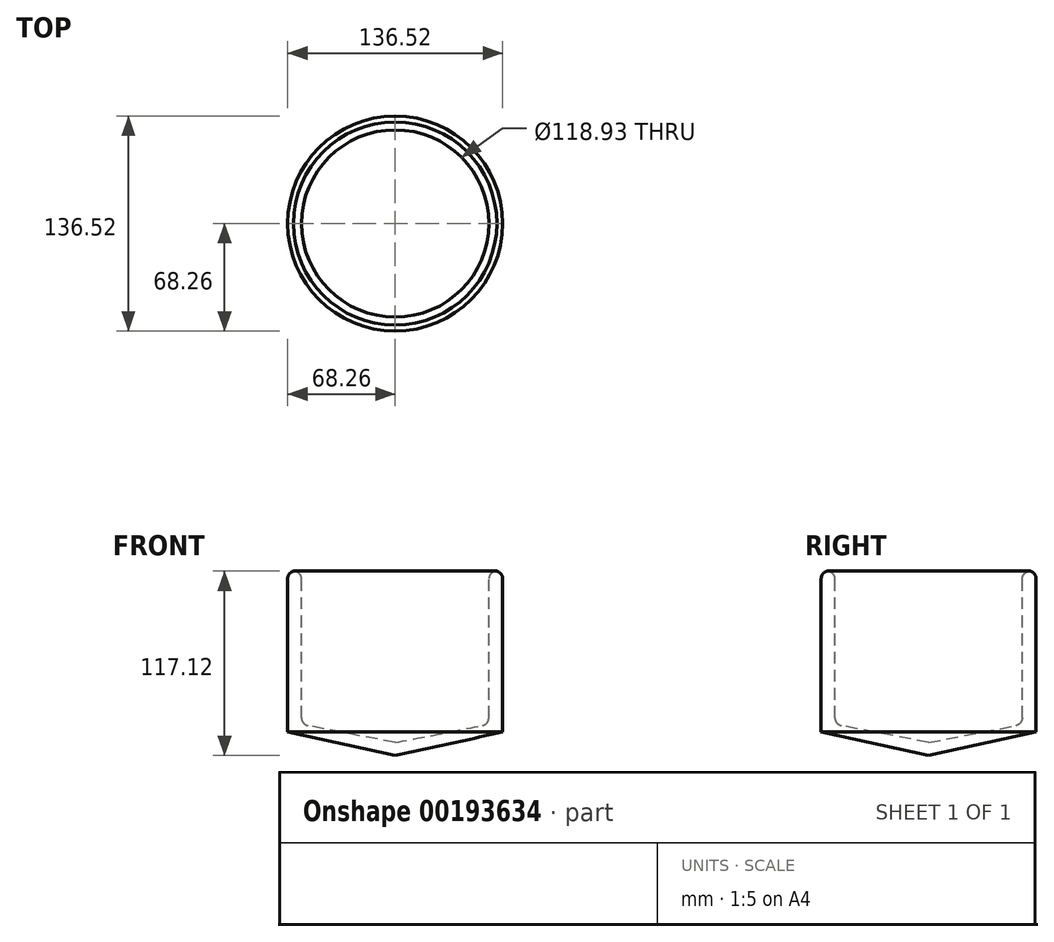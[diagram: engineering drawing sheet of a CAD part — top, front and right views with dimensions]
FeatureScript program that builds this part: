
annotation { "Feature Type Name" : "Feature", "Feature Type Description" : "" }
export const myFeature = defineFeature(function(context is Context, id is Id, definition is map)
    precondition{}
    {
        {
            var Q0;
            Q0=qCreatedBy(makeId("Front.planeOp"),FACE);
            var sketch = newSketch(context, id + "F0", { "sketchPlane" : qUnion([Q0])});
            skLineSegment(sketch, "E0", {"start": v(0, 62.05) * mm, "end": v(0, -60.22) * mm});
            skLineSegment(sketch, "E1", {"start": v(59.47, 48.7) * mm, "end": v(59.47, -48.7) * mm});
            skLineSegment(sketch, "E2", {"start": v(59.47, -48.7) * mm, "end": v(0, -60.22) * mm});
            skLineSegment(sketch, "E3", {"start": v(0, -68.42) * mm, "end": v(68.26, -53.55) * mm});
            skLineSegment(sketch, "E4", {"start": v(68.26, -53.55) * mm, "end": v(68.26, 48.7) * mm});
            skLineSegment(sketch, "E5", {"start": v(59.47, 48.7) * mm, "end": v(68.26, 48.7) * mm});
            skLineSegment(sketch, "E6", {"start": v(0, -60.22) * mm, "end": v(0, -68.42) * mm});
            skSolve(sketch);
        }
        {
            var Q0;
            Q0=makeQuery(id+"F0.imprint","IMPRINT",FACE,{"disambiguationData":[TD([[makeQuery(id+"F0.imprint","IMPRINT",EDGE,{"derivedFrom":sQuery(id+"F0.wireOp",EDGE,"E1")}),1.0]])]});
            var Q1;
            Q1=sQuery(id+"F0.wireOp",EDGE,"E0");
            revolve(context, id + "F1", {"entities" : qUnion([Q0]), "axis" : qUnion([Q1]), "revolveType" : RevolveType.FULL});
        }
        {
            var Q0;
            Q0=makeQuery(id+"F1.opRevolve","SWEPT_FACE",FACE,{"disambiguationData":[OSD([sQuery(id+"F0.wireOp",EDGE,"E2")])]});
            fillet(context, id + "F2", {"entities" : qUnion([Q0]), "radius" : 5.08 * mm, "tangentPropagation" : true, "allowEdgeOverflow" : false});
        }
        {
            var Q0;
            Q0=makeQuery(id+"F1.opRevolve","SWEPT_EDGE",EDGE,{"disambiguationData":[OSD([sQuery(id+"F0.wireOp",EDGE,"E1"),sQuery(id+"F0.wireOp",EDGE,"E5")])]});
            fillet(context, id + "F3", {"entities" : qUnion([Q0]), "radius" : 5.08 * mm, "tangentPropagation" : true, "allowEdgeOverflow" : false});
        }
        {
            var Q0;
            Q0=makeQuery(id+"F1.opRevolve","SWEPT_EDGE",EDGE,{"disambiguationData":[OSD([sQuery(id+"F0.wireOp",EDGE,"E4"),sQuery(id+"F0.wireOp",EDGE,"E5")])]});
            fillet(context, id + "F4", {"entities" : qUnion([Q0]), "radius" : 5.08 * mm, "tangentPropagation" : true, "allowEdgeOverflow" : false});
        }
    });
